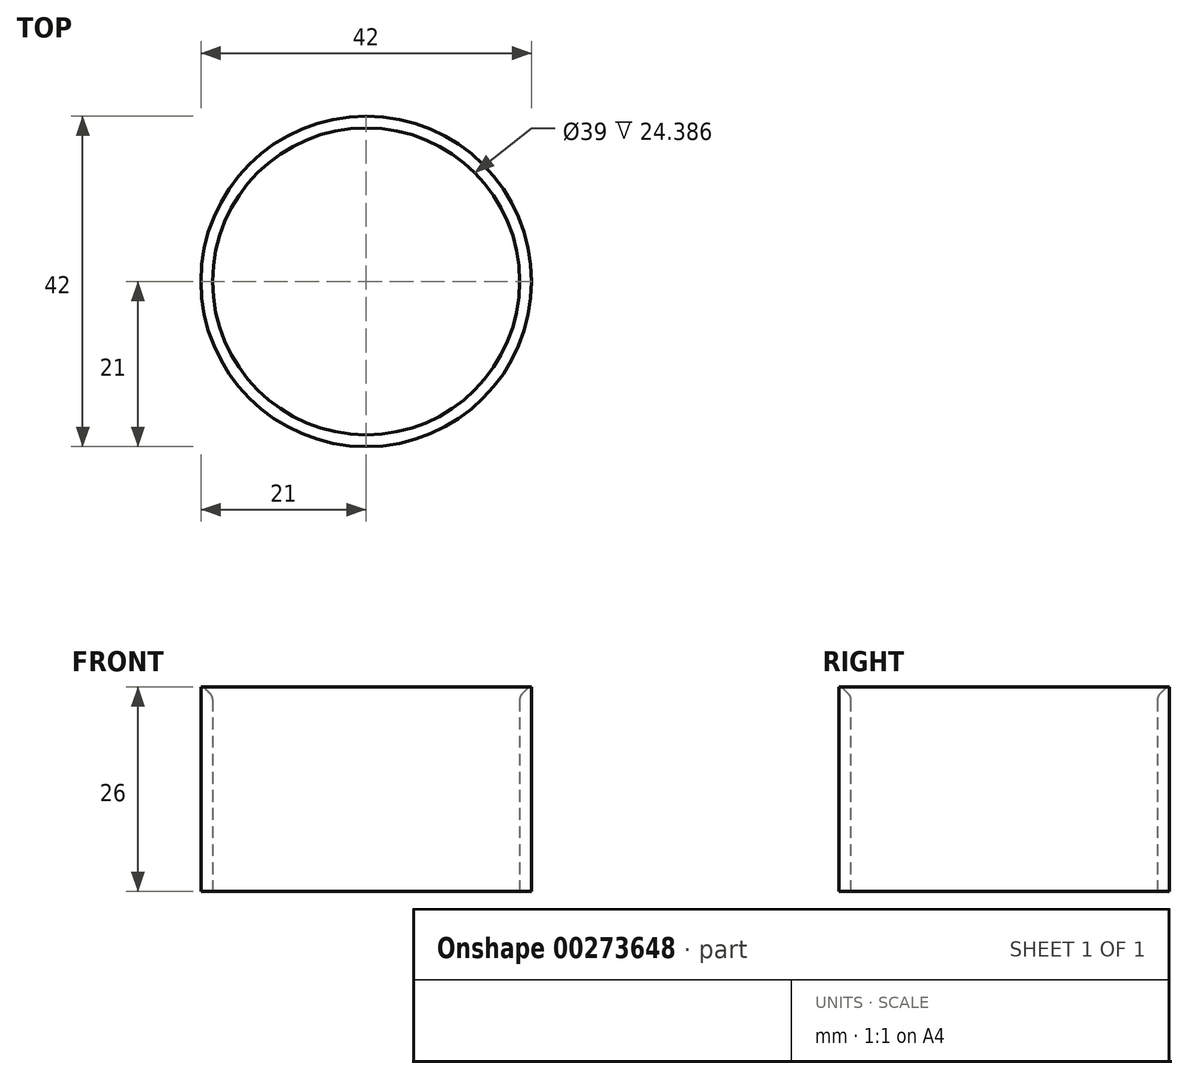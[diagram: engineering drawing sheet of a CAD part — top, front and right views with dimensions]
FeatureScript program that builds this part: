
annotation { "Feature Type Name" : "Feature", "Feature Type Description" : "" }
export const myFeature = defineFeature(function(context is Context, id is Id, definition is map)
    precondition{}
    {
        {
            var Q0;
            Q0=qCreatedBy(makeId("Top.planeOp"),FACE);
            var sketch = newSketch(context, id + "F0", { "sketchPlane" : qUnion([Q0])});
            skCircle(sketch, "E0", {"center": v(0, 0) * mm, "radius": 21 * mm});
            skCircle(sketch, "E1", {"center": v(0, 0) * mm, "radius": 19.5 * mm});
            skSolve(sketch);
        }
        {
            var Q0;
            Q0 = qSketchRegion(id + "F0", true);
            extrude(context, id + "F1", {"entities" : qUnion([Q0]), "depth" : 26 * mm, "offsetDistance" : 25 * mm});
        }
        {
            var Q0;
            Q0=makeQuery(id+"F1.opExtrude","CAP_EDGE",EDGE,{"disambiguationData":[OSD([sQuery(id+"F0.wireOp",EDGE,"E1")])],"isStart":false});
            chamfer(context, id + "F2", {"entities" : qUnion([Q0]), "width" : 1.2 * mm, "tangentPropagation" : true});
        }
        {
            var Q0;
            {var subQ0=sQuery(id+"F0.wireOp",EDGE,"E1");Q0=makeQuery(id+"F2.opChamfer","BLEND_EDGE",EDGE,{"blendedFrom":[makeQuery(id+"F1.opExtrude","CAP_EDGE",EDGE,{"disambiguationData":[OSD([subQ0])],"isStart":false}),makeQuery(id+"F1.opExtrude","CAP_FACE",FACE,{"disambiguationData":[OSD([sQuery(id+"F0.wireOp",EDGE,"E0"),subQ0])],"isStart":false})],"blendedInto":[makeQuery(id+"F1.opExtrude","CAP_FACE",FACE,{"disambiguationData":[OSD([sQuery(id+"F0.wireOp",EDGE,"E0"),subQ0])],"isStart":false})]});}
            fillet(context, id + "F3", {"entities" : qUnion([Q0]), "radius" : 0.3 * mm, "allowEdgeOverflow" : false});
        }
        {
            var Q0;
            {var subQ0=sQuery(id+"F0.wireOp",EDGE,"E1");Q0=makeQuery(id+"F2.opChamfer","BLEND_EDGE",EDGE,{"blendedFrom":[makeQuery(id+"F1.opExtrude","CAP_EDGE",EDGE,{"disambiguationData":[OSD([subQ0])],"isStart":false}),makeQuery(id+"F1.opExtrude","SWEPT_FACE",FACE,{"disambiguationData":[OSD([subQ0])]})],"blendedInto":[makeQuery(id+"F1.opExtrude","SWEPT_FACE",FACE,{"disambiguationData":[OSD([subQ0])]})]});}
            fillet(context, id + "F4", {"entities" : qUnion([Q0]), "radius" : 1 * mm, "tangentPropagation" : true, "allowEdgeOverflow" : false});
        }
    });
